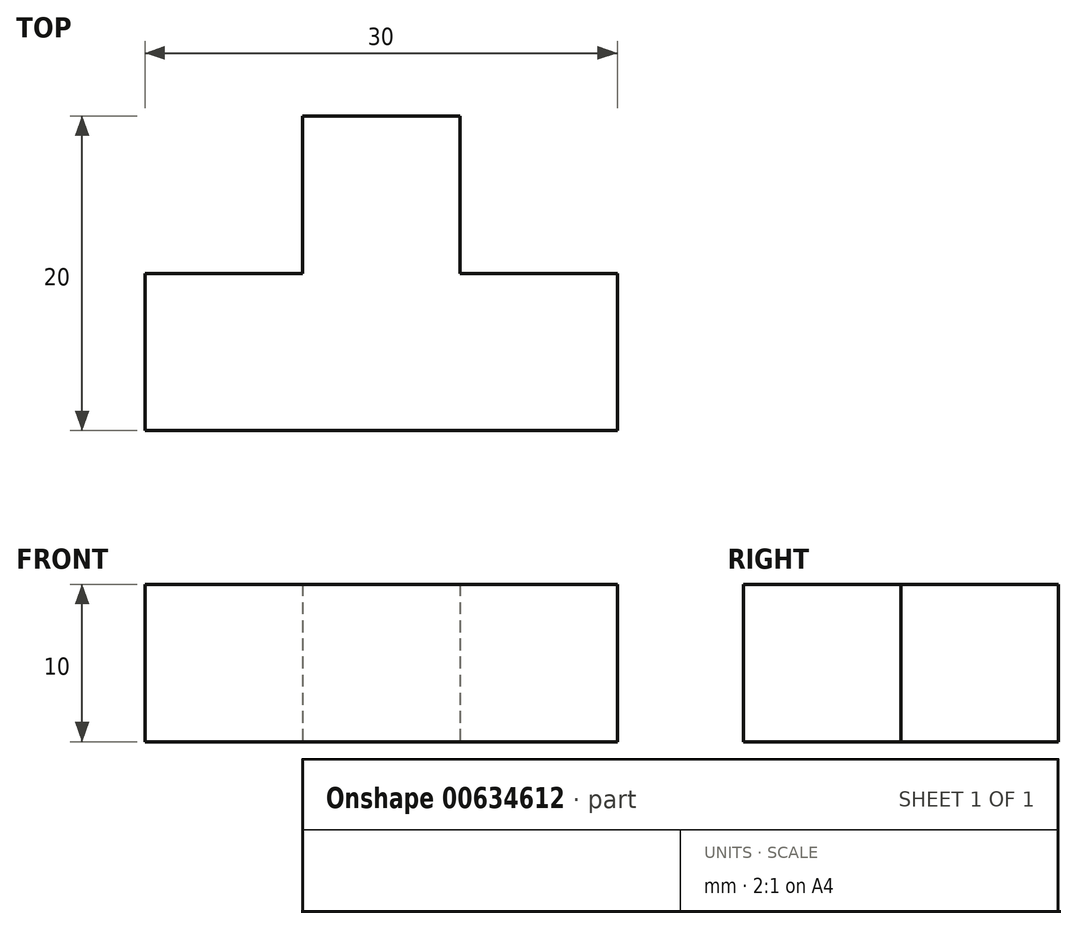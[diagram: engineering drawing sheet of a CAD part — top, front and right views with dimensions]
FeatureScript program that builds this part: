
annotation { "Feature Type Name" : "Feature", "Feature Type Description" : "" }
export const myFeature = defineFeature(function(context is Context, id is Id, definition is map)
    precondition{}
    {
        {
            var Q0;
            Q0=qCreatedBy(makeId("Top.planeOp"),FACE);
            var sketch = newSketch(context, id + "F0", { "sketchPlane" : qUnion([Q0])});
            skLineSegment(sketch, "E0.bottom", {"start": v(0, 0) * mm, "end": v(-30, 0) * mm});
            skLineSegment(sketch, "E0.top", {"start": v(0, 10) * mm, "end": v(-10, 10) * mm});
            skLineSegment(sketch, "E0.left", {"start": v(0, 0) * mm, "end": v(0, 10) * mm});
            skLineSegment(sketch, "E0.right", {"start": v(-30, 0) * mm, "end": v(-30, 10) * mm});
            skLineSegment(sketch, "E1", {"start": v(-20, 10) * mm, "end": v(-20, 20) * mm});
            skLineSegment(sketch, "E2", {"start": v(-20, 20) * mm, "end": v(-10, 20) * mm});
            skLineSegment(sketch, "E3", {"start": v(-10, 20) * mm, "end": v(-10, 10) * mm});
            skLineSegment(sketch, "E4.trimOffspring", {"start": v(-20, 10) * mm, "end": v(-30, 10) * mm});
            skSolve(sketch);
        }
        {
            var Q0;
            Q0 = qSketchRegion(id + "F0", true);
            extrude(context, id + "F1", {"entities" : qUnion([Q0]), "depth" : 10 * mm, "offsetDistance" : 25 * mm});
        }
    });
